# Revit family: ITK by ZPAS_Кабель-органайзер вертикальный_45U
name_source: partatom
category: Обобщенные модели
units: mm (PartAtom-declared; Revit-internal decimal feet)

## family parameters
Всегда вертикально = Да
Может служить основой для арматурных стержней = Нет
На основе рабочей плоскости = Нет
Общий = Нет
При загрузке вырезать с полостями = Нет
Размер круглого соединителя = Использовать диаметр
Тип детали = Нормальный
Точка расчета площади = Нет

## types (2) — shared parameters
ADSK_URL страницы изделия = https://www.itk-group.ru
ADSK_Версия Revit = 2019
ADSK_Версия семейства = 1.0
ADSK_Группирование = I. ЩИТЫ И ПУЛЬТЫ
ADSK_Единица измерения = шт
ADSK_Завод-изготовитель = IEK
ADSK_Марка = by ZPAS
ADSK_Масса = 6
ADSK_Материал наименование = Листовая сталь
IEK_URL = https://www.itk-group.ru
IEK_Описание = Крепится без инструментов к 19-дюймовым монтажным профилям.
IEK_Цена за единицу = 16548.28
KSI_CMa_Строительные материалы = 10.03.02.06
KSI_CPr_Строительные изделия = 61.1.04.08
URL = https://www.iek.ru
Высота = 1967 мм
Глубина = 44 мм
Изготовитель = ITK
Ширина = 80 мм

## per-type parameters (varying)
| type | ADSK_Код изделия | ADSK_Наименование | Материал |
| В1966,9_Черный | ZP-CC05-45U-V-0800 | ITK by ZPAS Кабель-органайзер вертикальный 45U 800 черный | Окраска - RAL 9005 |
| В1966,9_Серый | ZP-CC35-45U-V-0800 | ITK by ZPAS Кабель-органайзер вертикальный 45U 800 серый | Окраска - RAL 7035 |
